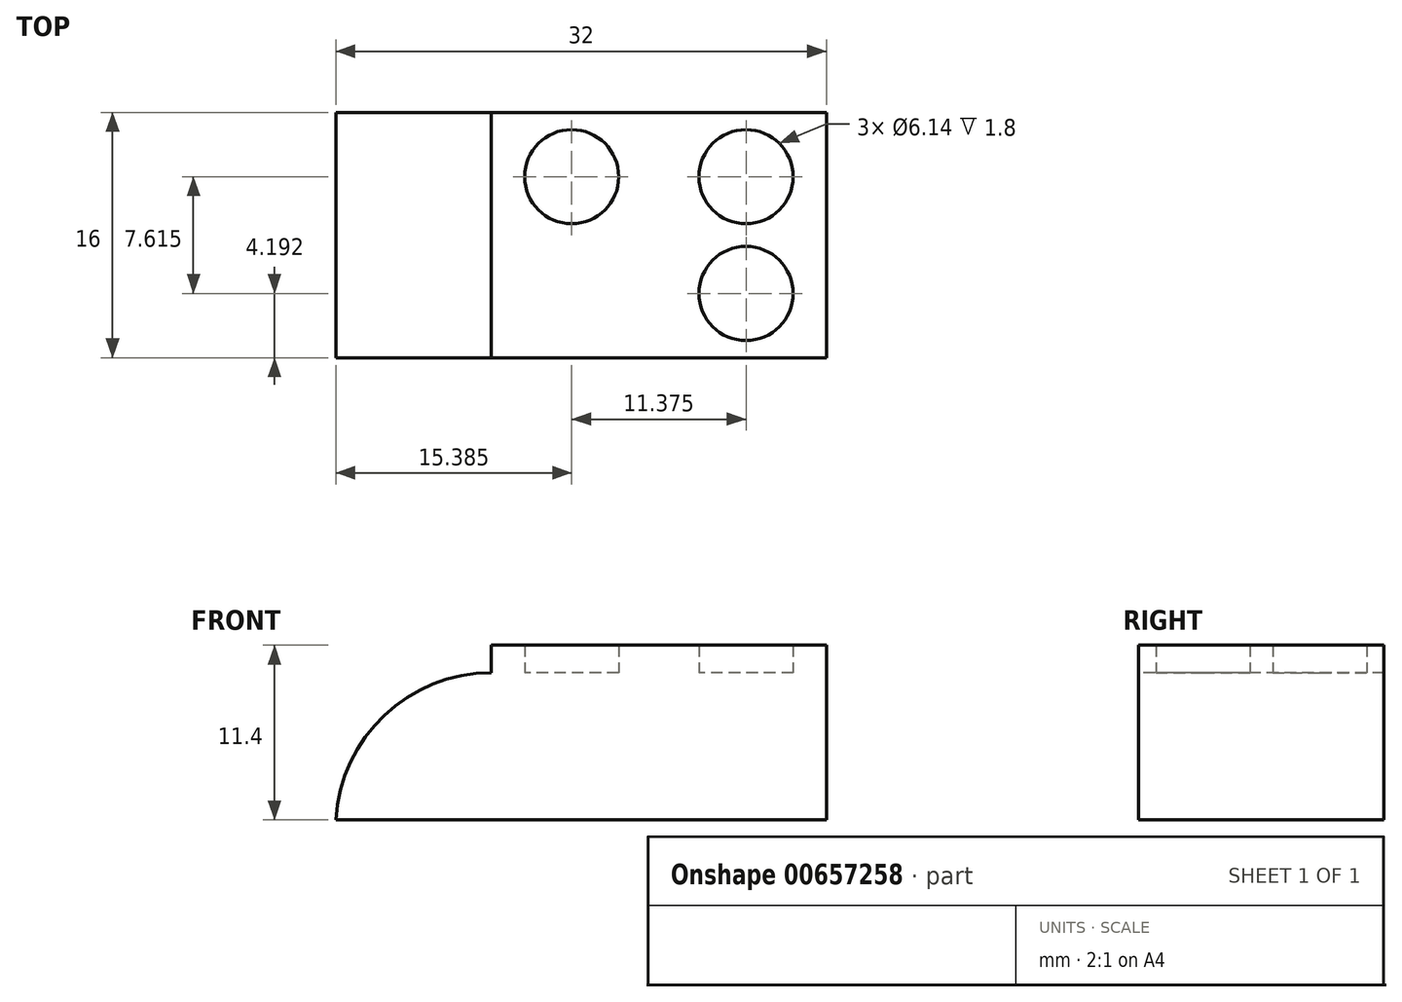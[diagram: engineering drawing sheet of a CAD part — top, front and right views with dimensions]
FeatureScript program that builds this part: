
annotation { "Feature Type Name" : "Feature", "Feature Type Description" : "" }
export const myFeature = defineFeature(function(context is Context, id is Id, definition is map)
    precondition{}
    {
        {
            var Q0;
            Q0=qCreatedBy(makeId("Top.planeOp"),FACE);
            var sketch = newSketch(context, id + "F0", { "sketchPlane" : qUnion([Q0])});
            skLineSegment(sketch, "E0.bottom", {"start": v(0, 0) * mm, "end": v(-32, 0) * mm});
            skLineSegment(sketch, "E0.top", {"start": v(0, 16) * mm, "end": v(-32, 16) * mm});
            skLineSegment(sketch, "E0.left", {"start": v(0, 0) * mm, "end": v(0, 16) * mm});
            skLineSegment(sketch, "E0.right", {"start": v(-32, 0) * mm, "end": v(-32, 16) * mm});
            skSolve(sketch);
        }
        {
            var Q0;
            Q0 = qSketchRegion(id + "F0", true);
            extrude(context, id + "F1", {"entities" : qUnion([Q0]), "depth" : 9.6 * mm, "offsetDistance" : 25.4 * mm});
        }
        {
            var Q0;
            Q0=makeQuery(id+"F1.opExtrude","CAP_EDGE",EDGE,{"disambiguationData":[OSD([sQuery(id+"F0.wireOp",EDGE,"E0.right")])],"isStart":false});
            fillet(context, id + "F2", {"entities" : qUnion([Q0]), "radius" : 10.16 * mm, "tangentPropagation" : true, "allowEdgeOverflow" : false});
        }
        {
            var Q0;
            Q0=makeQuery(id+"F1.opExtrude","CAP_FACE",FACE,{"disambiguationData":[OSD([sQuery(id+"F0.wireOp",EDGE,"E0.bottom"),sQuery(id+"F0.wireOp",EDGE,"E0.top"),sQuery(id+"F0.wireOp",EDGE,"E0.left"),sQuery(id+"F0.wireOp",EDGE,"E0.right")])],"isStart":false});
            var sketch = newSketch(context, id + "F3", { "sketchPlane" : qUnion([Q0])});
            skLineSegment(sketch, "E1", {"start": v(-21.86, 8) * mm, "end": v(0, 8) * mm, "construction": true});
            skLineSegment(sketch, "E2", {"start": v(-10.93, 16) * mm, "end": v(-10.93, 0) * mm, "construction": true});
            skCircle(sketch, "E3", {"center": v(-5.24, 11.8) * mm, "radius": 3.07 * mm});
            skCircle(sketch, "E4.MirrorC", {"center": v(-16.62, 11.8) * mm, "radius": 3.07 * mm});
            skLineSegment(sketch, "E5.MirrorCS", {"start": v(0, 8) * mm, "end": v(-21.86, 8) * mm, "construction": true});
            skCircle(sketch, "E6.MirrorC", {"center": v(-16.62, 4.2) * mm, "radius": 3.07 * mm});
            skCircle(sketch, "E7.MirrorC", {"center": v(-5.24, 4.2) * mm, "radius": 3.07 * mm});
            skSolve(sketch);
        }
        {
            var Q0;
            Q0=makeQuery(id+"F3.imprint","IMPRINT",FACE,{"disambiguationData":[TD([[makeQuery(id+"F3.imprint","IMPRINT",EDGE,{"derivedFrom":sQuery(id+"F3.wireOp",EDGE,"0630101b-2085-4ba3-9957-3241cde0ad420.MirrorC")}),-1.0]])]});
            var Q1;
            Q1=makeQuery(id+"F3.imprint","IMPRINT",FACE,{"disambiguationData":[TD([[makeQuery(id+"F3.imprint","IMPRINT",EDGE,{"derivedFrom":sQuery(id+"F3.wireOp",EDGE,"a65cdbcd-a581-47c8-b3eb-7786d89218010.MirrorC")}),-1.0]])]});
            var Q2;
            Q2=makeQuery(id+"F3.imprint","IMPRINT",FACE,{"disambiguationData":[TD([[makeQuery(id+"F3.imprint","IMPRINT",EDGE,{"derivedFrom":sQuery(id+"F3.wireOp",EDGE,"17c6536c-2235-4868-b63c-9eac11a5f24d0.MirrorC")}),1.0]])]});
            var Q3;
            Q3=makeQuery(id+"F3.imprint","IMPRINT",FACE,{"disambiguationData":[TD([[makeQuery(id+"F3.imprint","IMPRINT",EDGE,{"derivedFrom":sQuery(id+"F3.wireOp",EDGE,"Jy4rLTVo-phYC-2cNi-N1L6-CSAFYKBOofWX")}),1.0]])]});
            var Q4;
            Q4=makeQuery(id+"F3.imprint","IMPRINT",FACE,{"disambiguationData":[TD([[makeQuery(id+"F3.imprint","IMPRINT",EDGE,{"derivedFrom":sQuery(id+"F3.wireOp",EDGE,"E4.MirrorC")}),-1.0]])]});
            var Q5;
            Q5=makeQuery(id+"F3.imprint","IMPRINT",FACE,{"disambiguationData":[TD([[makeQuery(id+"F3.imprint","IMPRINT",EDGE,{"derivedFrom":sQuery(id+"F3.wireOp",EDGE,"E3")}),1.0]])]});
            var Q6;
            Q6=makeQuery(id+"F3.imprint","IMPRINT",FACE,{"disambiguationData":[TD([[makeQuery(id+"F3.imprint","IMPRINT",EDGE,{"derivedFrom":sQuery(id+"F3.wireOp",EDGE,"E6.MirrorC")}),1.0]])]});
            var Q7;
            Q7=makeQuery(id+"F3.imprint","IMPRINT",FACE,{"disambiguationData":[TD([[makeQuery(id+"F3.imprint","IMPRINT",EDGE,{"derivedFrom":sQuery(id+"F3.wireOp",EDGE,"E7.MirrorC")}),-1.0]])]});
            extrude(context, id + "F4", {"entities" : qUnion([Q0, Q1, Q2, Q3, Q4, Q5, Q6, Q7]), "operationType" : NewBodyOperationType.ADD, "depth" : 1.8 * mm, "offsetDistance" : 25.4 * mm});
        }
    });
